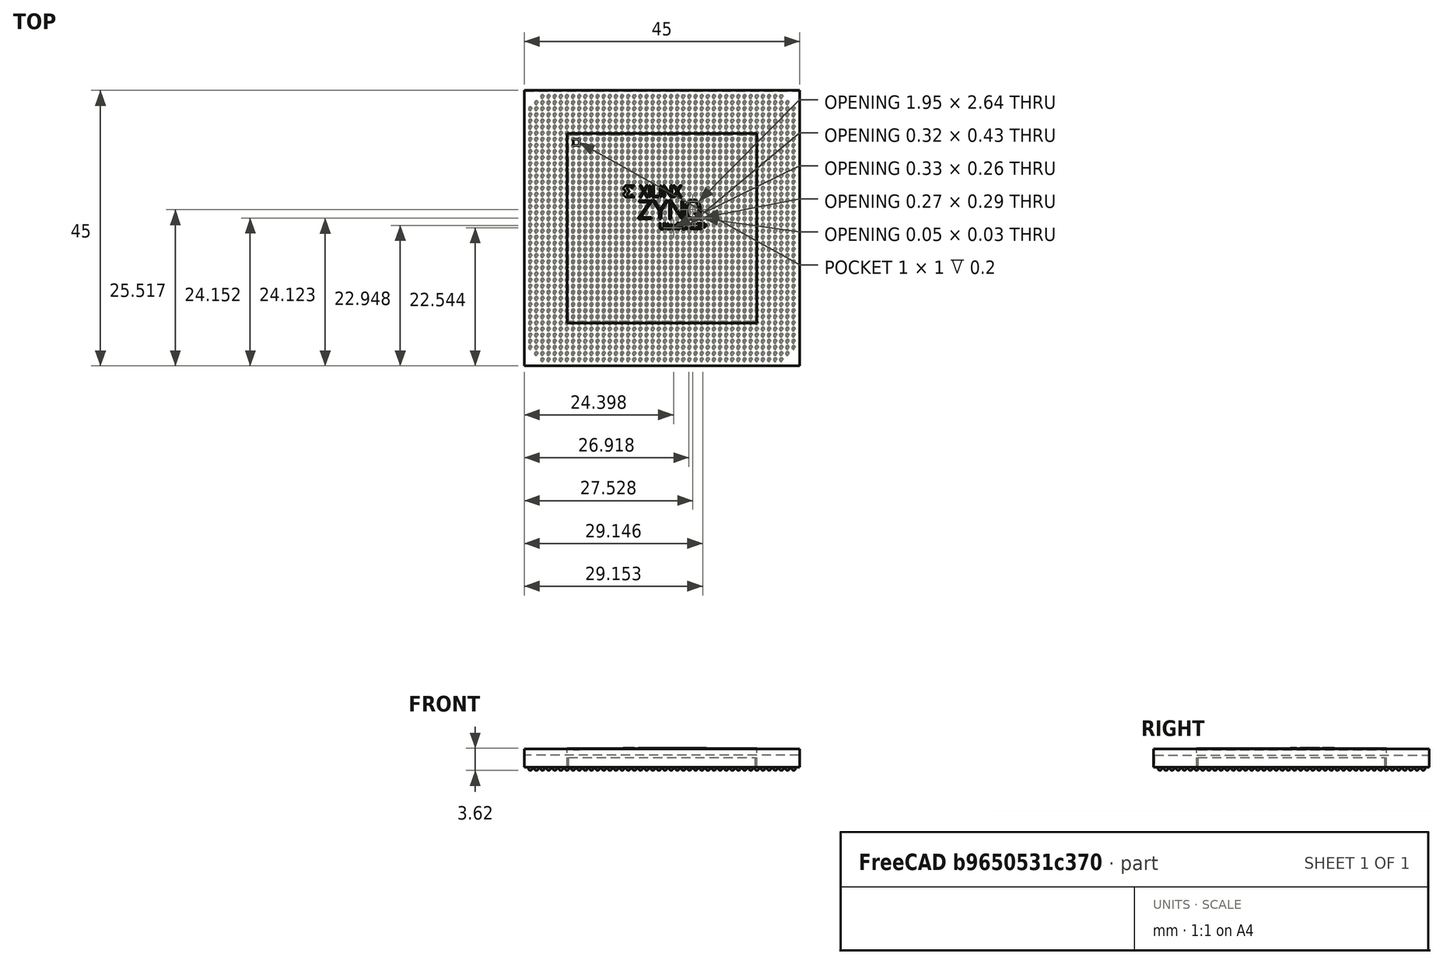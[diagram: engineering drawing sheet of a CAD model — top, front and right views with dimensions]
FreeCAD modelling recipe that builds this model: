
FCSTD DOCUMENT  (FreeCAD 0.21R33694 (Git))
Label: prueba
License: All rights reserved
LicenseURL: http://en.wikipedia.org/wiki/All_rights_reserved
objects: Part::Feature×4, Sketcher::SketchObject×3, PartDesign::Plane×3, PartDesign::Pad×2, PartDesign::Body×2, PartDesign::LinearPattern×2, App::Part×1, PartDesign::SubShapeBinder×1, PartDesign::AdditiveSphere×1, PartDesign::MultiTransform×1, PartDesign::Pocket×1, PartDesign::PolarPattern×1
note: 25 computed .brp shape members not serialized (recipe doc carries the construction recipe); baked Part::Feature solids carry a one-line shape summary decoded from their .brp

FEATURE [Part::Feature] Part__Feature  label="rotulo"
  Placement = pos=(-6.4,7,3.35) rot=(0,0,1;0rad)
  shape: bbox 13.62 x 7.193 x 0.01 mm, 597 faces, 25 solids (baked)
FEATURE [Part::Feature] Part__Feature001  label="BOLAS"
  shape: bbox 30.5 x 30.5 x 1.955 mm, 906 faces (baked)
FEATURE [Part::Feature] Part__Feature002  label="cuadrado_concuadrado"
  shape: bbox 31 x 31 x 3.01 mm, 11 faces (baked)
FEATURE [Part::Feature] Part__Feature003  label="punto"
  shape: bbox 30.5 x 30.5 x 0.1 mm, 6 faces (baked)
FEATURE [App::Part] Unnamed
  Group = -> [Part__Feature,Part__Feature001,Part__Feature002,Part__Feature003]
  Origin = -> Origin
FEATURE [Sketcher::SketchObject] Sketch
  FullyConstrained = true
  MapMode = 5
  Support = -> [XY_Plane002]
  sketch-geometry (4):
    g0: LineSegment StartX=-22.5 StartY=-22.5 StartZ=0 EndX=22.5 EndY=-22.5 EndZ=0
    g1: LineSegment StartX=22.5 StartY=-22.5 StartZ=0 EndX=22.5 EndY=22.5 EndZ=0
    g2: LineSegment StartX=22.5 StartY=22.5 StartZ=0 EndX=-22.5 EndY=22.5 EndZ=0
    g3: LineSegment StartX=-22.5 StartY=22.5 StartZ=0 EndX=-22.5 EndY=-22.5 EndZ=0
  constraints (11):
    c: Coincident(g0,g1)
    c: Coincident(g1,g2)
    c: Coincident(g2,g3)
    c: Coincident(g3,g0)
    c: Horizontal(g0)
    c: Horizontal(g2)
    c: Vertical(g1)
    c: Vertical(g3)
    c: Symmetric(g0,g1,g-1)
    c: Equal(g2,g1)
    c: DistanceY(g1,g1) = 45
FEATURE [PartDesign::Pad] Pad
  Direction = (0,0,1)
  Length = 3.01
  Length2 = 10
  Profile = -> Sketch
  ReferenceAxis = -> Sketch [N_Axis]
  Reversed = true
  Type = 0
FEATURE [PartDesign::Body] Body001  label="Cuerpo"
  Group = -> [Sketch,Pad]
  Origin = -> Origin002
  Placement = pos=(0,0,3.25) rot=(0,0,1;0rad)
  Tip = -> Pad
FEATURE [PartDesign::SubShapeBinder] Binder
  BindCopyOnChange = 0
  BindMode = 0
  ClaimChildren = false
  Context = -> Body [Binder.]
  Fuse = false
  MakeFace = true
  OffsetFill = false
  OffsetIntersection = false
  OffsetJoinType = 0
  OffsetOpenResult = false
  PartialLoad = false
  Relative = true
  Support = -> [Body001]
  _Version = 2
FEATURE [PartDesign::Plane] DatumPlane
  AttachmentOffset = pos=(0,0,-1) rot=(0,0,1;0rad)
  Length = 60
  MapMode = 5
  Placement = pos=(0,0,2.25) rot=(0,0,1;0rad)
  ResizeMode = 0
  Support = -> [Binder]
  Width = 60
FEATURE [Sketcher::SketchObject] Sketch001
  ExternalGeometry = -> [Binder]
  FullyConstrained = true
  MapMode = 5
  Placement = pos=(0,0,2.25) rot=(0,0,1;0rad)
  Support = -> [DatumPlane]
  sketch-geometry (4):
    g0: LineSegment StartX=22.4 StartY=-22.4 StartZ=0 EndX=-22.4 EndY=-22.4 EndZ=0
    g1: LineSegment StartX=-22.4 StartY=-22.4 StartZ=0 EndX=-22.4 EndY=22.4 EndZ=0
    g2: LineSegment StartX=-22.4 StartY=22.4 StartZ=0 EndX=22.4 EndY=22.4 EndZ=0
    g3: LineSegment StartX=22.4 StartY=22.4 StartZ=0 EndX=22.4 EndY=-22.4 EndZ=0
  constraints (11):
    c: Coincident(g0,g1)
    c: Coincident(g1,g2)
    c: Coincident(g2,g3)
    c: Coincident(g3,g0)
    c: Horizontal(g0)
    c: Horizontal(g2)
    c: Vertical(g1)
    c: Vertical(g3)
    c: Symmetric(g1,g0,g-1)
    c: Equal(g1,g2)
    c: DistanceX(g-3,g1) = 0.1
FEATURE [PartDesign::Plane] DatumPlane001
  AttachmentOffset = pos=(0,0,-0.03) rot=(0,0,1;0rad)
  Length = 60
  MapMode = 5
  Placement = pos=(0,0,0.27) rot=(1,0,0;3.14159rad)
  ResizeMode = 0
  Support = -> [Binder]
  Width = 60
FEATURE [PartDesign::Pad] Pad001
  Direction = (0,0,1)
  Length = 10
  Length2 = 10
  Placement = pos=(0,0,2.25) rot=(0,0,1;0rad)
  Profile = -> Sketch001
  ReferenceAxis = -> Sketch001 [N_Axis]
  Type = 3
  UpToFace = -> DatumPlane001 [Plane]
FEATURE [PartDesign::Plane] DatumPlane002
  AttachmentOffset = pos=(0,0,0.2) rot=(0,0,1;0rad)
  Length = 60
  MapMode = 5
  Placement = pos=(0,0,0.04) rot=(1,0,0;3.14159rad)
  ResizeMode = 0
  Support = -> [Binder]
  Width = 60
FEATURE [PartDesign::AdditiveSphere] Sphere
  Angle1 = -90
  Angle2 = 90
  Angle3 = 360
  AttacherType = Attacher::AttachEngine3D
  AttachmentOffset = pos=(-21.5,-21.5,0) rot=(0,0,1;0rad)
  BaseFeature = -> Pad001
  MapMode = 5
  Placement = pos=(-21.5,21.5,0.04) rot=(1,0,0;3.14159rad)
  Radius = 0.3
  Support = -> [DatumPlane002]
FEATURE [PartDesign::LinearPattern] LinearPattern
  Direction = -> X_Axis003
  Length = 43
  Occurrences = 44
  Placement = pos=(-21.5,21.5,0.04) rot=(1,0,0;3.14159rad)
FEATURE [PartDesign::LinearPattern] LinearPattern001
  Direction = -> Y_Axis003
  Length = 43
  Occurrences = 44
  Placement = pos=(-21.5,21.5,0.04) rot=(1,0,0;3.14159rad)
  Reversed = true
FEATURE [PartDesign::MultiTransform] MultiTransform
  BaseFeature = -> Sphere
  Originals = -> [Sphere]
  Placement = pos=(-21.5,21.5,0.04) rot=(1,0,0;3.14159rad)
  Transformations = -> [LinearPattern,LinearPattern001]
FEATURE [Sketcher::SketchObject] Sketch002
  FullyConstrained = false
  MapMode = 5
  Placement = pos=(-21.5,21.5,0.27) rot=(1,0,0;3.14159rad)
  Support = -> [MultiTransform]
  sketch-geometry (6):
    g0: LineSegment StartX=0.453989 StartY=42.5466 StartZ=0 EndX=1.50525 EndY=42.5466 EndZ=0
    g1: LineSegment StartX=1.50525 StartY=42.5466 StartZ=0 EndX=1.50525 EndY=43.7474 EndZ=0
    g2: LineSegment StartX=1.50525 StartY=43.7474 StartZ=0 EndX=-0.730165 EndY=43.7474 EndZ=0
    g3: LineSegment StartX=-0.730165 StartY=43.7474 StartZ=0 EndX=-0.730165 EndY=41.5707 EndZ=0
    g4: LineSegment StartX=-0.730165 StartY=41.5707 StartZ=0 EndX=0.453989 EndY=41.5707 EndZ=0
    g5: LineSegment StartX=0.453989 StartY=41.5707 StartZ=0 EndX=0.453989 EndY=42.5466 EndZ=0
  constraints (12):
    c: Horizontal(g0)
    c: Coincident(g0,g1)
    c: Vertical(g1)
    c: Coincident(g1,g2)
    c: Horizontal(g2)
    c: Coincident(g2,g3)
    c: Vertical(g3)
    c: Coincident(g3,g4)
    c: Horizontal(g4)
    c: Coincident(g4,g5)
    c: Coincident(g5,g0)
    c: Vertical(g5)
FEATURE [PartDesign::Pocket] Pocket
  BaseFeature = -> MultiTransform
  Direction = (0,-1e-16,1)
  Length = 5
  Length2 = 5
  Placement = pos=(-21.5,21.5,0.04) rot=(1,0,0;3.14159rad)
  Profile = -> Sketch002
  ReferenceAxis = -> Sketch002 [N_Axis]
  Reversed = true
  Type = 0
FEATURE [PartDesign::PolarPattern] PolarPattern
  Angle = 360
  Axis = -> Z_Axis003
  BaseFeature = -> Pocket
  Occurrences = 4
  Originals = -> [Pocket]
  Placement = pos=(-21.5,21.5,0.04) rot=(1,0,0;3.14159rad)
FEATURE [PartDesign::Body] Body  label="bolas"
  Group = -> [Binder,DatumPlane,Sketch001,DatumPlane001,Pad001,DatumPlane002,Sphere,MultiTransform,LinearPattern,LinearPattern001,Sketch002,Pocket,PolarPattern]
  Origin = -> Origin003
  Tip = -> PolarPattern
